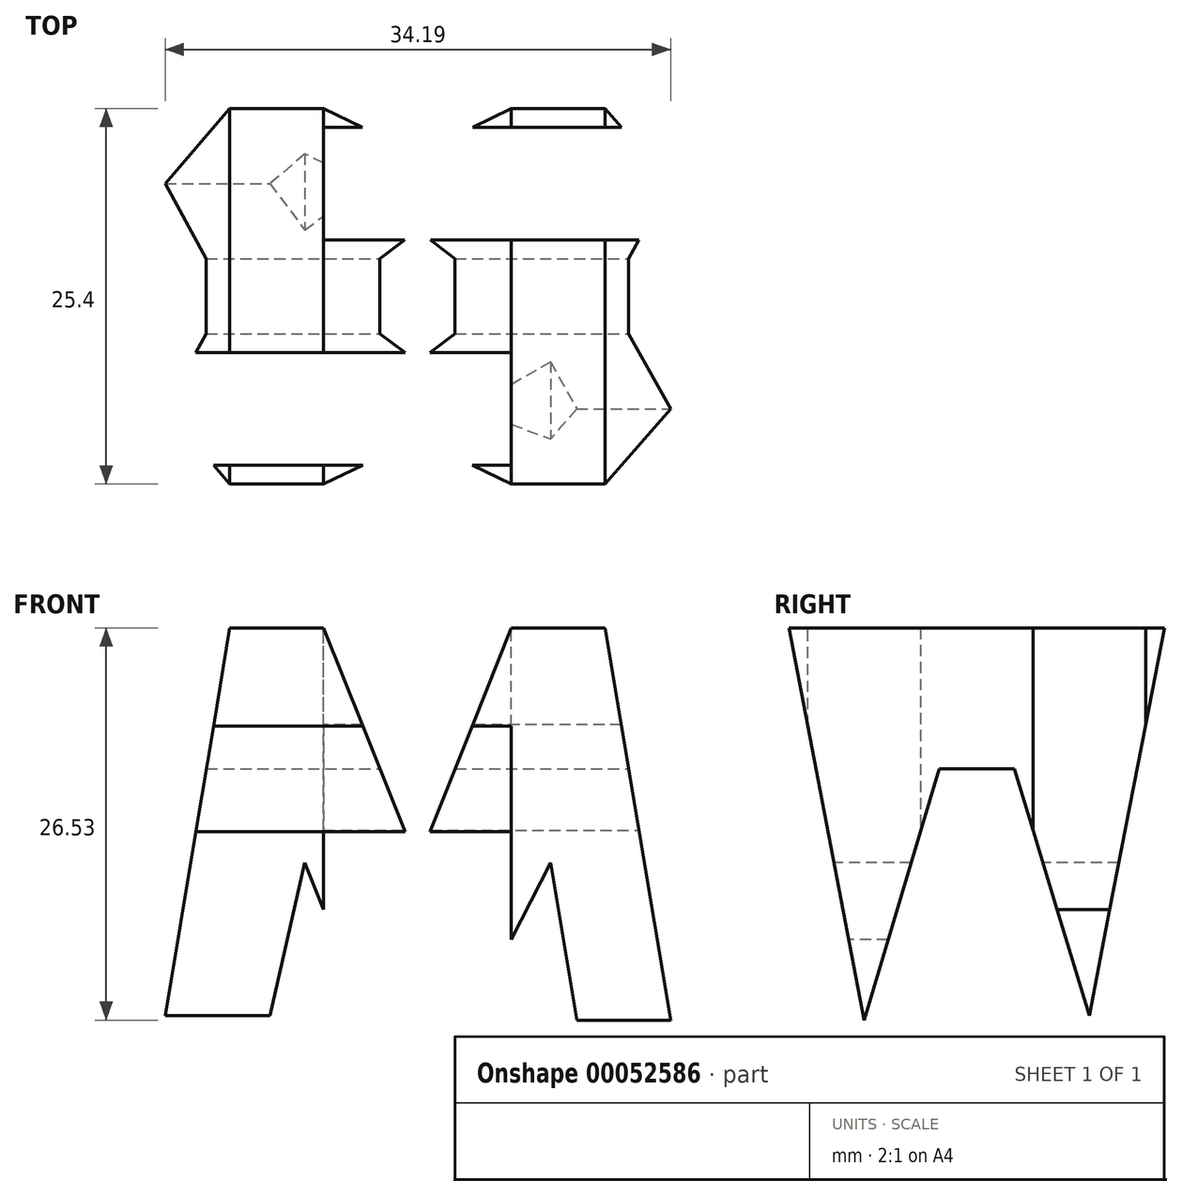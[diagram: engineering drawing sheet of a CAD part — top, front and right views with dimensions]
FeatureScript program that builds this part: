
annotation { "Feature Type Name" : "Feature", "Feature Type Description" : "" }
export const myFeature = defineFeature(function(context is Context, id is Id, definition is map)
    precondition{}
    {
        {
            var Q0;
            Q0=qCreatedBy(makeId("Front.planeOp"),FACE);
            var sketch = newSketch(context, id + "F0", { "sketchPlane" : qUnion([Q0])});
            skLineSegment(sketch, "E0", {"start": v(0, 0) * mm, "end": v(38.1, 0) * mm});
            skLineSegment(sketch, "E1", {"start": v(38.1, 0) * mm, "end": v(38.1, 38.1) * mm});
            skLineSegment(sketch, "E2", {"start": v(38.1, 38.1) * mm, "end": v(0, 38.1) * mm});
            skLineSegment(sketch, "E3", {"start": v(0, 38.1) * mm, "end": v(0, 0) * mm});
            skSolve(sketch);
        }
        {
            var Q0;
            Q0=makeQuery(id+"F0.imprint","IMPRINT",FACE,{"disambiguationData":[TD([[makeQuery(id+"F0.imprint","IMPRINT",EDGE,{"derivedFrom":sQuery(id+"F0.wireOp",EDGE,"E0")}),1.0]])]});
            extrude(context, id + "F1", {"entities" : qUnion([Q0]), "depth" : 38.1 * mm});
        }
        {
            var Q0;
            Q0=qCreatedBy(makeId("Front.planeOp"),FACE);
            cPlane(context, id + "F2", {"entities" : qUnion([Q0]), "cplaneType" : CPlaneType.OFFSET, "offset" : 38.1 * mm, "width" : 152.4 * mm, "height" : 152.4 * mm});
        }
        {
            var Q0;
            Q0=qCreatedBy(makeId("Right.planeOp"),FACE);
            cPlane(context, id + "F3", {"entities" : qUnion([Q0]), "cplaneType" : CPlaneType.OFFSET, "offset" : 38.1 * mm, "width" : 152.4 * mm, "height" : 152.4 * mm});
        }
        {
            var Q0;
            Q0=qCreatedBy(makeId("Top.planeOp"),FACE);
            cPlane(context, id + "F4", {"entities" : qUnion([Q0]), "cplaneType" : CPlaneType.OFFSET, "offset" : 38.1 * mm, "width" : 152.4 * mm, "height" : 152.4 * mm});
        }
        {
            var Q0;
            Q0=qCreatedBy(id+"F3.planeOp",FACE);
            var sketch = newSketch(context, id + "F5", { "sketchPlane" : qUnion([Q0])});
            skLineSegment(sketch, "E4.bottom", {"start": v(0, 0) * mm, "end": v(-38.1, 0) * mm});
            skLineSegment(sketch, "E4.top", {"start": v(0, 38.1) * mm, "end": v(-38.1, 38.1) * mm});
            skLineSegment(sketch, "E4.left", {"start": v(0, 0) * mm, "end": v(0, 38.1) * mm});
            skLineSegment(sketch, "E4.right", {"start": v(-38.1, 0) * mm, "end": v(-38.1, 38.1) * mm});
            skLineSegment(sketch, "E5", {"start": v(-38.1, 38.1) * mm, "end": v(-31.75, 0) * mm});
            skLineSegment(sketch, "E6", {"start": v(-31.75, 0) * mm, "end": v(-25.4, 0) * mm});
            skLineSegment(sketch, "E7", {"start": v(-25.4, 0) * mm, "end": v(-19.05, 15.88) * mm});
            skLineSegment(sketch, "E8", {"start": v(-19.05, 15.88) * mm, "end": v(-12.7, 0) * mm});
            skLineSegment(sketch, "E9", {"start": v(-12.7, 0) * mm, "end": v(-6.35, 0) * mm});
            skLineSegment(sketch, "E10", {"start": v(-6.35, 0) * mm, "end": v(0, 38.1) * mm});
            skLineSegment(sketch, "E11", {"start": v(0, 38.1) * mm, "end": v(-6.35, 38.1) * mm});
            skLineSegment(sketch, "E12", {"start": v(-6.35, 38.1) * mm, "end": v(-11.43, 11.89) * mm});
            skLineSegment(sketch, "E13", {"start": v(-11.43, 11.89) * mm, "end": v(-16.51, 28.58) * mm});
            skLineSegment(sketch, "E14", {"start": v(-16.51, 28.58) * mm, "end": v(-21.59, 28.58) * mm});
            skLineSegment(sketch, "E15", {"start": v(-21.6, 28.58) * mm, "end": v(-26.67, 11.57) * mm});
            skLineSegment(sketch, "E16", {"start": v(-26.67, 11.57) * mm, "end": v(-31.75, 38.1) * mm});
            skLineSegment(sketch, "E17", {"start": v(-31.75, 38.1) * mm, "end": v(-38.1, 38.1) * mm});
            skSolve(sketch);
        }
        {
            var Q0;
            Q0=makeQuery(id+"F5.imprint","IMPRINT",FACE,{"disambiguationData":[TD([[makeQuery(id+"F5.imprint","IMPRINT",EDGE,{"derivedFrom":sQuery(id+"F5.wireOp",EDGE,"E4.top")}),1.0]])]});
            var Q1;
            {var subQ0=sQuery(id+"F5.wireOp",EDGE,"E4.right");Q1=makeQuery(id+"F5.imprint","IMPRINT",FACE,{"disambiguationData":[TD([[makeQuery(id+"F5.imprint","IMPRINT",EDGE,{"derivedFrom":subQ0}),-1.0]])]});}
            var Q2;
            {var subQ0=sQuery(id+"F5.wireOp",EDGE,"E7");Q2=makeQuery(id+"F5.imprint","IMPRINT",FACE,{"disambiguationData":[TD([[makeQuery(id+"F5.imprint","IMPRINT",EDGE,{"derivedFrom":subQ0}),-1.0]])]});}
            var Q3;
            {var subQ0=sQuery(id+"F5.wireOp",EDGE,"E4.left");Q3=makeQuery(id+"F5.imprint","IMPRINT",FACE,{"disambiguationData":[TD([[makeQuery(id+"F5.imprint","IMPRINT",EDGE,{"derivedFrom":subQ0}),1.0]])]});}
            extrude(context, id + "F6", {"entities" : qUnion([Q0, Q1, Q2, Q3]), "operationType" : NewBodyOperationType.REMOVE, "oppositeDirection" : true, "depth" : 38.1 * mm});
        }
        {
            var Q0;
            Q0=qCreatedBy(id+"F2.planeOp",FACE);
            var sketch = newSketch(context, id + "F7", { "sketchPlane" : qUnion([Q0])});
            skLineSegment(sketch, "E18", {"start": v(0, 0) * mm, "end": v(0, 38.1) * mm});
            skLineSegment(sketch, "E19", {"start": v(0, 38.1) * mm, "end": v(38.1, 38.1) * mm});
            skLineSegment(sketch, "E20", {"start": v(38.1, 38.1) * mm, "end": v(38.1, 0) * mm});
            skLineSegment(sketch, "E21", {"start": v(38.1, 0) * mm, "end": v(0, 0) * mm});
            skLineSegment(sketch, "E22", {"start": v(0, 0) * mm, "end": v(6.35, 38.1) * mm});
            skLineSegment(sketch, "E23", {"start": v(6.35, 38.1) * mm, "end": v(12.7, 38.1) * mm});
            skLineSegment(sketch, "E24", {"start": v(12.7, 38.1) * mm, "end": v(19.05, 22.22) * mm});
            skLineSegment(sketch, "E25", {"start": v(19.05, 22.22) * mm, "end": v(25.4, 38.1) * mm});
            skLineSegment(sketch, "E26", {"start": v(25.4, 38.1) * mm, "end": v(31.75, 38.1) * mm});
            skLineSegment(sketch, "E27", {"start": v(31.75, 38.1) * mm, "end": v(38.1, 0) * mm});
            skLineSegment(sketch, "E28", {"start": v(38.1, 0) * mm, "end": v(38.1, 0) * mm});
            skLineSegment(sketch, "E29", {"start": v(28.05, 22.22) * mm, "end": v(21.59, 9.52) * mm});
            skLineSegment(sketch, "E30", {"start": v(21.59, 9.52) * mm, "end": v(16.51, 9.52) * mm});
            skLineSegment(sketch, "E31", {"start": v(16.51, 9.52) * mm, "end": v(11.43, 22.23) * mm});
            skLineSegment(sketch, "E32", {"start": v(11.43, 22.23) * mm, "end": v(6.35, 0) * mm});
            skLineSegment(sketch, "E33", {"start": v(6.35, 0) * mm, "end": v(0, 0) * mm});
            skLineSegment(sketch, "E34", {"start": v(28.05, 22.23) * mm, "end": v(31.75, 0) * mm});
            skSolve(sketch);
        }
        {
            var Q0;
            {var subQ0=sQuery(id+"F7.wireOp",EDGE,"E24");Q0=makeQuery(id+"F7.imprint","IMPRINT",FACE,{"disambiguationData":[TD([[makeQuery(id+"F7.imprint","IMPRINT",EDGE,{"derivedFrom":subQ0}),1.0]])]});}
            var Q1;
            {var subQ0=sQuery(id+"F7.wireOp",EDGE,"E18");Q1=makeQuery(id+"F7.imprint","IMPRINT",FACE,{"disambiguationData":[TD([[makeQuery(id+"F7.imprint","IMPRINT",EDGE,{"derivedFrom":subQ0}),-1.0]])]});}
            var Q2;
            Q2=makeQuery(id+"F7.imprint","IMPRINT",FACE,{"disambiguationData":[TD([[makeQuery(id+"F7.imprint","IMPRINT",EDGE,{"derivedFrom":sQuery(id+"F7.wireOp",EDGE,"E29")}),1.0]])]});
            var Q3;
            {var subQ0=sQuery(id+"F7.wireOp",EDGE,"E20");Q3=makeQuery(id+"F7.imprint","IMPRINT",FACE,{"disambiguationData":[TD([[makeQuery(id+"F7.imprint","IMPRINT",EDGE,{"derivedFrom":subQ0}),-1.0]])]});}
            extrude(context, id + "F8", {"entities" : qUnion([Q0, Q1, Q2, Q3]), "operationType" : NewBodyOperationType.REMOVE, "oppositeDirection" : true, "depth" : 38.1 * mm});
        }
        {
            var Q0;
            Q0=qCreatedBy(id+"F4.planeOp",FACE);
            var sketch = newSketch(context, id + "F9", { "sketchPlane" : qUnion([Q0])});
            skLineSegment(sketch, "E35.bottom", {"start": v(0, 0) * mm, "end": v(38.1, 0) * mm});
            skLineSegment(sketch, "E35.top", {"start": v(0, -38.1) * mm, "end": v(38.1, -38.1) * mm});
            skLineSegment(sketch, "E35.left", {"start": v(0, 0) * mm, "end": v(0, -38.1) * mm});
            skLineSegment(sketch, "E35.right", {"start": v(38.1, 0) * mm, "end": v(38.1, -38.1) * mm});
            skLineSegment(sketch, "E36", {"start": v(38.1, -7.62) * mm, "end": v(12.7, -7.62) * mm});
            skLineSegment(sketch, "E37", {"start": v(12.7, -7.62) * mm, "end": v(12.7, -15.24) * mm});
            skLineSegment(sketch, "E38", {"start": v(12.7, -15.24) * mm, "end": v(38.1, -15.24) * mm});
            skLineSegment(sketch, "E39", {"start": v(0, -22.86) * mm, "end": v(25.4, -22.86) * mm});
            skLineSegment(sketch, "E40", {"start": v(25.4, -22.86) * mm, "end": v(25.4, -30.48) * mm});
            skLineSegment(sketch, "E41", {"start": v(25.4, -30.48) * mm, "end": v(0, -30.48) * mm});
            skSolve(sketch);
        }
        {
            var Q0;
            {var subQ0=sQuery(id+"F9.wireOp",EDGE,"E36");Q0=makeQuery(id+"F9.imprint","IMPRINT",FACE,{"disambiguationData":[TD([[makeQuery(id+"F9.imprint","IMPRINT",EDGE,{"derivedFrom":subQ0}),1.0]])]});}
            var Q1;
            {var subQ0=sQuery(id+"F9.wireOp",EDGE,"E39");Q1=makeQuery(id+"F9.imprint","IMPRINT",FACE,{"disambiguationData":[TD([[makeQuery(id+"F9.imprint","IMPRINT",EDGE,{"derivedFrom":subQ0}),-1.0]])]});}
            extrude(context, id + "F10", {"entities" : qUnion([Q0, Q1]), "operationType" : NewBodyOperationType.REMOVE, "oppositeDirection" : true, "depth" : 38.1 * mm});
        }
    });
